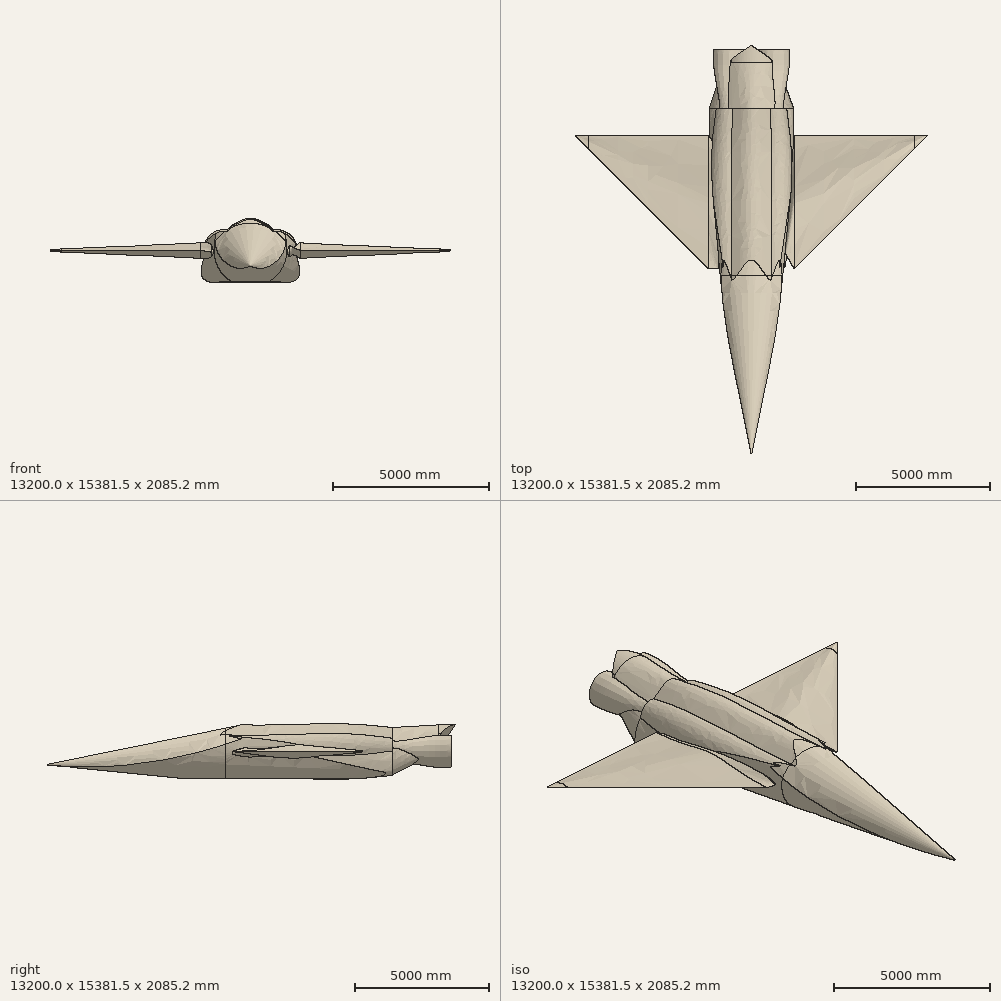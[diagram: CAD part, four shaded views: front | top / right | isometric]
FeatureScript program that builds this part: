
annotation { "Feature Type Name" : "Feature", "Feature Type Description" : "" }
export const myFeature = defineFeature(function(context is Context, id is Id, definition is map)
    precondition{}
    {
        {
            var Q0;
            Q0=qCreatedBy(makeId("Front.planeOp"),FACE);
            cPlane(context, id + "F0", {"entities" : qUnion([Q0]), "cplaneType" : CPlaneType.OFFSET, "offset" : 1750 * mm, "width" : 152.4 * mm, "height" : 152.4 * mm});
        }
        {
            var Q0;
            Q0=qCreatedBy(id+"F0.planeOp",FACE);
            var sketch = newSketch(context, id + "F1", { "sketchPlane" : qUnion([Q0])});
            skLineSegment(sketch, "E0.top", {"start": v(-1394.2, -1000) * mm, "end": v(1394.2, -1000) * mm});
            skPoint(sketch, "E0.middle", {"position": v(0, 0) * mm});
            skFitSpline(sketch, "E1", {"points": [v(-1600, -1000) * mm, v(-848, 530) * mm, v(0, 1000) * mm, v(848, 530) * mm, v(1600, -1000) * mm], "startDerivative": vector(0, 10524.75) * mm, "endDerivative": vector(0, -10524.75) * mm});
            skArc(sketch, "E2", {"start": v(-735.27, 618.52) * mm, "mid": v(-1273.27, 435.52) * mm, "end": v(-1440.68, -107.53) * mm});
            skArc(sketch, "E3.trimOffspring", {"start": v(1440.68, -107.53) * mm, "mid": v(1273.27, 435.52) * mm, "end": v(735.27, 618.52) * mm});
            skFitSpline(sketch, "E4.trimOffspring", {"points": [v(-1600, -1000) * mm, v(-848, 530) * mm, v(0, 1000) * mm, v(848, 530) * mm, v(1600, -1000) * mm], "startDerivative": vector(0, 10524.75) * mm, "endDerivative": vector(0, -10524.75) * mm});
            skFitSpline(sketch, "E5.trimOffspring", {"points": [v(-1600, -1000) * mm, v(-848, 530) * mm, v(0, 1000) * mm, v(848, 530) * mm, v(1600, -1000) * mm], "startDerivative": vector(0, 10524.75) * mm, "endDerivative": vector(0, -10524.75) * mm});
            skArc(sketch, "E6.filletArc", {"start": v(-1593.82, -787.83) * mm, "mid": v(-1539.85, -937.05) * mm, "end": v(-1394.2, -1000) * mm});
            skArc(sketch, "E7.filletArc", {"start": v(1394.2, -1000) * mm, "mid": v(1539.85, -937.05) * mm, "end": v(1593.82, -787.83) * mm});
            skSolve(sketch);
        }
        {
            var Q0;
            Q0=qCreatedBy(makeId("Front.planeOp"),FACE);
            var sketch = newSketch(context, id + "F2", { "sketchPlane" : qUnion([Q0])});
            skLineSegment(sketch, "E8.top", {"start": v(-1394.2, -1000) * mm, "end": v(1394.2, -1000) * mm});
            skPoint(sketch, "E8.middle", {"position": v(0, 0) * mm});
            skFitSpline(sketch, "E9", {"points": [v(-1600, -1000) * mm, v(-848, 530) * mm, v(0, 1000) * mm, v(848, 530) * mm, v(1600, -1000) * mm], "startDerivative": vector(0, 10524.75) * mm, "endDerivative": vector(0, -10524.75) * mm});
            skArc(sketch, "E10", {"start": v(-735.27, 618.52) * mm, "mid": v(-1273.27, 435.52) * mm, "end": v(-1440.68, -107.53) * mm});
            skArc(sketch, "E11.trimOffspring", {"start": v(1440.68, -107.53) * mm, "mid": v(1273.27, 435.52) * mm, "end": v(735.27, 618.52) * mm});
            skFitSpline(sketch, "E12.trimOffspring", {"points": [v(-1600, -1000) * mm, v(-848, 530) * mm, v(0, 1000) * mm, v(848, 530) * mm, v(1600, -1000) * mm], "startDerivative": vector(0, 10524.75) * mm, "endDerivative": vector(0, -10524.75) * mm});
            skFitSpline(sketch, "E13.trimOffspring", {"points": [v(-1600, -1000) * mm, v(-848, 530) * mm, v(0, 1000) * mm, v(848, 530) * mm, v(1600, -1000) * mm], "startDerivative": vector(0, 10524.75) * mm, "endDerivative": vector(0, -10524.75) * mm});
            skArc(sketch, "E14.filletArc", {"start": v(-1593.82, -787.83) * mm, "mid": v(-1539.85, -937.05) * mm, "end": v(-1394.2, -1000) * mm});
            skArc(sketch, "E15.filletArc", {"start": v(1394.2, -1000) * mm, "mid": v(1539.85, -937.05) * mm, "end": v(1593.82, -787.83) * mm});
            skSolve(sketch);
        }
        {
            var Q0;
            Q0=qCreatedBy(makeId("Front.planeOp"),FACE);
            cPlane(context, id + "F3", {"entities" : qUnion([Q0]), "cplaneType" : CPlaneType.OFFSET, "offset" : 3500 * mm, "oppositeDirection" : true, "width" : 150 * mm, "height" : 150 * mm});
        }
        {
            var Q0;
            Q0=qCreatedBy(id+"F3.planeOp",FACE);
            var sketch = newSketch(context, id + "F4", { "sketchPlane" : qUnion([Q0])});
            skLineSegment(sketch, "E16.top", {"start": v(-1394.2, -1000) * mm, "end": v(1394.2, -1000) * mm});
            skPoint(sketch, "E16.middle", {"position": v(0, 0) * mm});
            skFitSpline(sketch, "E17", {"points": [v(-1600, -1000) * mm, v(-848, 530) * mm, v(0, 1000) * mm, v(848, 530) * mm, v(1600, -1000) * mm], "startDerivative": vector(0, 10524.75) * mm, "endDerivative": vector(0, -10524.75) * mm});
            skArc(sketch, "E18", {"start": v(-735.27, 618.52) * mm, "mid": v(-1273.27, 435.52) * mm, "end": v(-1440.68, -107.53) * mm});
            skArc(sketch, "E19.trimOffspring", {"start": v(1440.68, -107.53) * mm, "mid": v(1273.27, 435.52) * mm, "end": v(735.27, 618.52) * mm});
            skFitSpline(sketch, "E20.trimOffspring", {"points": [v(-1600, -1000) * mm, v(-848, 530) * mm, v(0, 1000) * mm, v(848, 530) * mm, v(1600, -1000) * mm], "startDerivative": vector(0, 10524.75) * mm, "endDerivative": vector(0, -10524.75) * mm});
            skFitSpline(sketch, "E21.trimOffspring", {"points": [v(-1600, -1000) * mm, v(-848, 530) * mm, v(0, 1000) * mm, v(848, 530) * mm, v(1600, -1000) * mm], "startDerivative": vector(0, 10524.75) * mm, "endDerivative": vector(0, -10524.75) * mm});
            skArc(sketch, "E22.filletArc", {"start": v(-1593.82, -787.83) * mm, "mid": v(-1539.85, -937.05) * mm, "end": v(-1394.2, -1000) * mm});
            skArc(sketch, "E23.filletArc", {"start": v(1394.2, -1000) * mm, "mid": v(1539.85, -937.05) * mm, "end": v(1593.82, -787.83) * mm});
            skSolve(sketch);
        }
        {
            var Q0;
            Q0=qCreatedBy(makeId("Front.planeOp"),FACE);
            cPlane(context, id + "F5", {"entities" : qUnion([Q0]), "cplaneType" : CPlaneType.OFFSET, "offset" : 4500 * mm, "oppositeDirection" : true, "width" : 150 * mm, "height" : 150 * mm});
        }
        {
            var Q0;
            Q0=qCreatedBy(id+"F5.planeOp",FACE);
            var sketch = newSketch(context, id + "F6", { "sketchPlane" : qUnion([Q0])});
            skLineSegment(sketch, "E24.top", {"start": v(-1413.07, -900) * mm, "end": v(1413.07, -900) * mm});
            skPoint(sketch, "E24.middle", {"position": v(0, 0) * mm});
            skFitSpline(sketch, "E25", {"points": [v(-1600, -900) * mm, v(-784.42, 441.24) * mm, v(0, 900) * mm, v(784.42, 441.24) * mm, v(1600, -900) * mm], "startDerivative": vector(0, 9508.62) * mm, "endDerivative": vector(0, -9508.62) * mm});
            skArc(sketch, "E26", {"start": v(-719.25, 488.69) * mm, "mid": v(-1131.76, 394.84) * mm, "end": v(-1324.66, 18.33) * mm});
            skArc(sketch, "E27.trimOffspring", {"start": v(1324.66, 18.33) * mm, "mid": v(1131.76, 394.84) * mm, "end": v(719.25, 488.69) * mm});
            skFitSpline(sketch, "E28.trimOffspring", {"points": [v(-1600, -900) * mm, v(-784.42, 441.24) * mm, v(0, 900) * mm, v(784.42, 441.24) * mm, v(1600, -900) * mm], "startDerivative": vector(0, 9508.62) * mm, "endDerivative": vector(0, -9508.62) * mm});
            skFitSpline(sketch, "E29.trimOffspring", {"points": [v(-1600, -900) * mm, v(-784.42, 441.24) * mm, v(0, 900) * mm, v(784.42, 441.24) * mm, v(1600, -900) * mm], "startDerivative": vector(0, 9508.62) * mm, "endDerivative": vector(0, -9508.62) * mm});
            skArc(sketch, "E30.filletArc", {"start": v(-1592.48, -705.43) * mm, "mid": v(-1545.4, -842.02) * mm, "end": v(-1413.07, -900) * mm});
            skArc(sketch, "E31.filletArc", {"start": v(1413.07, -900) * mm, "mid": v(1545.4, -842.02) * mm, "end": v(1592.48, -705.43) * mm});
            skLineSegment(sketch, "E32", {"start": v(-719.25, 488.69) * mm, "end": v(-1324.66, 18.33) * mm, "construction": true});
            skLineSegment(sketch, "E33", {"start": v(719.25, 488.69) * mm, "end": v(1324.66, 18.33) * mm, "construction": true});
            skSolve(sketch);
        }
        {
            var Q0;
            Q0=qCreatedBy(makeId("Front.planeOp"),FACE);
            cPlane(context, id + "F7", {"entities" : qUnion([Q0]), "cplaneType" : CPlaneType.OFFSET, "offset" : 6232.05 * mm, "oppositeDirection" : true, "width" : 150 * mm, "height" : 150 * mm});
        }
        {
            var Q0;
            Q0=qCreatedBy(id+"F7.planeOp",FACE);
            var sketch = newSketch(context, id + "F8", { "sketchPlane" : qUnion([Q0])});
            skArc(sketch, "E34", {"start": v(998.61, 52.63) * mm, "mid": v(0, 1000) * mm, "end": v(-998.61, 52.63) * mm});
            skLineSegment(sketch, "E35", {"start": v(0, 0) * mm, "end": v(-948.68, 0) * mm});
            skLineSegment(sketch, "E36", {"start": v(0, 0) * mm, "end": v(948.68, 0) * mm});
            skPoint(sketch, "E37.visualSharp", {"position": v(-1000, 0) * mm});
            skArc(sketch, "E37.filletArc", {"start": v(-998.61, 52.63) * mm, "mid": v(-984.96, 15.59) * mm, "end": v(-948.68, 0) * mm});
            skPoint(sketch, "E38.visualSharp", {"position": v(1000, 0) * mm});
            skArc(sketch, "E38.filletArc", {"start": v(948.68, 0) * mm, "mid": v(984.96, 15.59) * mm, "end": v(998.61, 52.63) * mm});
            skLineSegment(sketch, "E39", {"start": v(0, 1000) * mm, "end": v(0, 675) * mm, "construction": true});
            skPoint(sketch, "E39.endSnap0", {"position": v(0, 1000) * mm});
            skLineSegment(sketch, "E40", {"start": v(0, 675) * mm, "end": v(737.82, 675) * mm, "construction": true});
            skLineSegment(sketch, "E41", {"start": v(0, 675) * mm, "end": v(-737.82, 675) * mm, "construction": true});
            skSolve(sketch);
        }
        {
            var Q0;
            Q0=qSketchRegion(id+"F1",true);
            var Q1;
            Q1=qSketchRegion(id+"F2",true);
            var Q2;
            Q2=qSketchRegion(id+"F4",true);
            var Q3;
            Q3=qSketchRegion(id+"F6",true);
            loft(context, id + "F9", {"sheetProfilesArray" : [{ "sheetProfileEntities" : qUnion([Q0]) }, { "sheetProfileEntities" : qUnion([Q1]) }, { "sheetProfileEntities" : qUnion([Q2]) }, { "sheetProfileEntities" : qUnion([Q3]) }]});
        }
        {
            var Q0;
            Q0=sQuery(id+"F6.wireOp",EDGE,"E32");
            var Q1;
            Q1=sQuery(id+"F8.wireOp",VERTEX,"E41.end");
            cPlane(context, id + "F10", {"entities" : qUnion([Q0, Q1]), "cplaneType" : CPlaneType.LINE_ANGLE, "offset" : 25 * mm, "angle" : 0 * degree, "width" : 150 * mm, "height" : 150 * mm});
        }
        {
            var Q0;
            Q0=qCreatedBy(id+"F10.planeOp",FACE);
            var sketch = newSketch(context, id + "F11", { "sketchPlane" : qUnion([Q0])});
            skLineSegment(sketch, "E42", {"start": v(-589.34, -4526.34) * mm, "end": v(-612.8, -6268.32) * mm});
            skLineSegment(sketch, "E43", {"start": v(-1354.08, -4472.19) * mm, "end": v(-612.8, -6268.32) * mm});
            skSolve(sketch);
        }
        {
            var Q0;
            Q0=sQuery(id+"F6.wireOp",EDGE,"E33");
            var Q1;
            Q1=sQuery(id+"F8.wireOp",VERTEX,"E40.end");
            cPlane(context, id + "F12", {"entities" : qUnion([Q0, Q1]), "cplaneType" : CPlaneType.LINE_ANGLE, "offset" : 25 * mm, "angle" : 0 * degree, "width" : 150 * mm, "height" : 150 * mm});
        }
        {
            var Q0;
            Q0=qCreatedBy(id+"F12.planeOp",FACE);
            var sketch = newSketch(context, id + "F13", { "sketchPlane" : qUnion([Q0])});
            skLineSegment(sketch, "E44", {"start": v(589.34, 4526.34) * mm, "end": v(612.8, 6268.32) * mm});
            skLineSegment(sketch, "E45", {"start": v(1354.08, 4472.19) * mm, "end": v(612.8, 6268.32) * mm});
            skSolve(sketch);
        }
        {
            var Q1;
            Q1=makeQuery(id+"F6.imprint","IMPRINT",FACE,{"disambiguationData":[TD([[makeQuery(id+"F6.imprint","IMPRINT",EDGE,{"derivedFrom":sQuery(id+"F6.wireOp",EDGE,"E24.top")}),1.0]])]});
            var Q2;
            Q2=makeQuery(id+"F8.imprint","IMPRINT",FACE,{"disambiguationData":[TD([[makeQuery(id+"F8.imprint","IMPRINT",EDGE,{"derivedFrom":sQuery(id+"F8.wireOp",EDGE,"E34")}),1.0]])]});
            var Q3;
            Q3=sQuery(id+"F11.wireOp",EDGE,"E42");
            var Q4;
            Q4=sQuery(id+"F13.wireOp",EDGE,"E44");
            loft(context, id + "F14", {"operationType" : NewBodyOperationType.ADD, "addGuides" : true, "sheetProfilesArray" : [{ "sheetProfileEntities" : qUnion([Q1]) }, { "sheetProfileEntities" : qUnion([Q2]) }], "guidesArray" : [{ "guideEntities" : qUnion([Q3]), "guideDerivativeType" : LoftGuideDerivativeType.DEFAULT, "guideDerivativeMagnitude" : 1 }, { "guideEntities" : qUnion([Q4]), "guideDerivativeType" : LoftGuideDerivativeType.DEFAULT, "guideDerivativeMagnitude" : 1 }]});
        }
        {
            var Q0;
            Q0=makeQuery(id+"F14.opLoft","CAP_FACE",FACE,{"disambiguationData":[OSD([makeQuery(id+"F8.imprint","IMPRINT",FACE,{"disambiguationData":[TD([[makeQuery(id+"F8.imprint","IMPRINT",EDGE,{"derivedFrom":sQuery(id+"F8.wireOp",EDGE,"E34")}),1.0]])]})])],"isStart":true});
            extrude(context, id + "F15", {"entities" : qUnion([Q0]), "operationType" : NewBodyOperationType.ADD, "depth" : 649.4 * mm});
        }
        {
            var Q0;
            Q0=qCreatedBy(makeId("Right.planeOp"),FACE);
            var sketch = newSketch(context, id + "F16", { "sketchPlane" : qUnion([Q0])});
            skLineSegment(sketch, "E46", {"start": v(0, 0) * mm, "end": v(4500, 0) * mm});
            skLineSegment(sketch, "E47", {"start": v(4500, 0) * mm, "end": v(6232.05, 0) * mm});
            skLineSegment(sketch, "E48", {"start": v(4500, 0) * mm, "end": v(4500, 1000) * mm});
            skLineSegment(sketch, "E49", {"start": v(4500, 1000) * mm, "end": v(6881.46, 1000) * mm});
            skLineSegment(sketch, "E50", {"start": v(6881.46, 1000) * mm, "end": v(6881.46, -1000) * mm});
            skLineSegment(sketch, "E51", {"start": v(6881.46, 1000) * mm, "end": v(6232.05, 0) * mm});
            skLineSegment(sketch, "E52", {"start": v(6232.05, 0) * mm, "end": v(5582.64, -1000) * mm});
            skLineSegment(sketch, "E53", {"start": v(5582.64, -1000) * mm, "end": v(6881.46, -1000) * mm});
            skSolve(sketch);
        }
        {
            var Q0;
            Q0=makeQuery(id+"F16.imprint","IMPRINT",FACE,{"disambiguationData":[TD([[makeQuery(id+"F16.imprint","IMPRINT",EDGE,{"derivedFrom":sQuery(id+"F16.wireOp",EDGE,"E50")}),-1.0]])]});
            var Q1;
            Q1=sQuery(id+"F16.wireOp",EDGE,"E49");
            revolve(context, id + "F17", {"operationType" : NewBodyOperationType.REMOVE, "entities" : qUnion([Q0]), "axis" : qUnion([Q1]), "revolveType" : RevolveType.SYMMETRIC, "oppositeDirection" : true, "angle" : 182 * degree});
        }
        {
            var Q0;
            Q0=makeQuery(id+"F9.opLoft","CAP_FACE",FACE,{"disambiguationData":[OSD([makeQuery(id+"F1.imprint","IMPRINT",FACE,{"disambiguationData":[TD([[makeQuery(id+"F1.imprint","IMPRINT",EDGE,{"derivedFrom":sQuery(id+"F1.wireOp",EDGE,"E0.top")}),1.0]])]})])],"isStart":true});
            extrude(context, id + "F18", {"entities" : qUnion([Q0]), "depth" : 6750 * mm});
        }
        {
            var Q0;
            Q0=qCreatedBy(makeId("Right.planeOp"),FACE);
            var sketch = newSketch(context, id + "F19", { "sketchPlane" : qUnion([Q0])});
            skLineSegment(sketch, "E54", {"start": v(0, 0) * mm, "end": v(-3500, 0) * mm});
            skLineSegment(sketch, "E55", {"start": v(-3500, 0) * mm, "end": v(-3500, -1000) * mm});
            skLineSegment(sketch, "E56", {"start": v(-3500, -1000) * mm, "end": v(-8500, -1000) * mm});
            skLineSegment(sketch, "E57", {"start": v(-8500, -1000) * mm, "end": v(-8500, -499.31) * mm});
            skLineSegment(sketch, "E58", {"start": v(-1151.4, 0) * mm, "end": v(-1151.4, 1000) * mm});
            skLineSegment(sketch, "E59", {"start": v(-1151.4, 1000) * mm, "end": v(-8500, -499.31) * mm});
            skLineSegment(sketch, "E60", {"start": v(-8500, -499.31) * mm, "end": v(-3500, -1000) * mm});
            skLineSegment(sketch, "E61", {"start": v(-1151.4, 1000) * mm, "end": v(-8500, 1000) * mm});
            skLineSegment(sketch, "E62", {"start": v(-8500, 1000) * mm, "end": v(-8500, -499.31) * mm});
            skLineSegment(sketch, "E63", {"start": v(-8500, -1000) * mm, "end": v(-8500, -1980) * mm});
            skLineSegment(sketch, "E64", {"start": v(-3500, -1000) * mm, "end": v(6286.5, -1980) * mm});
            skLineSegment(sketch, "E65", {"start": v(6286.5, -1980) * mm, "end": v(-8500, -1980) * mm});
            skLineSegment(sketch, "E66", {"start": v(-8500, -499.31) * mm, "end": v(-3500, -499.31) * mm});
            skSolve(sketch);
        }
        {
            var Q0;
            Q0=makeQuery(id+"F19.imprint","IMPRINT",FACE,{"disambiguationData":[TD([[makeQuery(id+"F19.imprint","IMPRINT",EDGE,{"derivedFrom":sQuery(id+"F19.wireOp",EDGE,"E59")}),-1.0]])]});
            var Q1;
            Q1=sQuery(id+"F19.wireOp",EDGE,"E66");
            revolve(context, id + "F20", {"operationType" : NewBodyOperationType.REMOVE, "entities" : qUnion([Q0]), "axis" : qUnion([Q1]), "revolveType" : RevolveType.SYMMETRIC, "oppositeDirection" : true, "angle" : 250 * degree});
        }
        {
            var Q0;
            Q0=makeQuery(id+"F19.imprint","IMPRINT",FACE,{"disambiguationData":[TD([[makeQuery(id+"F19.imprint","IMPRINT",EDGE,{"derivedFrom":sQuery(id+"F19.wireOp",EDGE,"E56")}),-1.0]])]});
            var Q1;
            Q1=makeQuery(id+"F19.imprint","IMPRINT",FACE,{"disambiguationData":[TD([[makeQuery(id+"F19.imprint","IMPRINT",EDGE,{"derivedFrom":sQuery(id+"F19.wireOp",EDGE,"E56")}),1.0]])]});
            var Q2;
            Q2=sQuery(id+"F19.wireOp",EDGE,"E54");
            revolve(context, id + "F21", {"operationType" : NewBodyOperationType.REMOVE, "entities" : qUnion([Q0, Q1]), "axis" : qUnion([Q2]), "revolveType" : RevolveType.SYMMETRIC, "oppositeDirection" : true, "angle" : 240 * degree});
        }
        {
            var Q0;
            Q0=qCreatedBy(makeId("Front.planeOp"),FACE);
            cPlane(context, id + "F22", {"entities" : qUnion([Q0]), "cplaneType" : CPlaneType.OFFSET, "offset" : 3500 * mm, "oppositeDirection" : true, "width" : 150 * mm, "height" : 150 * mm});
        }
        {
            var Q0;
            Q0=qCreatedBy(id+"F22.planeOp",FACE);
            var sketch = newSketch(context, id + "F23", { "sketchPlane" : qUnion([Q0])});
            skCircle(sketch, "E67", {"center": v(-825, 0) * mm, "radius": 600 * mm});
            skCircle(sketch, "E68", {"center": v(825, 0) * mm, "radius": 600 * mm});
            skSolve(sketch);
        }
        {
            var Q0;
            Q0=qCreatedBy(makeId("Front.planeOp"),FACE);
            cPlane(context, id + "F24", {"entities" : qUnion([Q0]), "cplaneType" : CPlaneType.OFFSET, "offset" : 4500 * mm, "oppositeDirection" : true, "width" : 150 * mm, "height" : 150 * mm});
        }
        {
            var Q0;
            Q0=qCreatedBy(id+"F24.planeOp",FACE);
            var sketch = newSketch(context, id + "F25", { "sketchPlane" : qUnion([Q0])});
            skCircle(sketch, "E69", {"center": v(-825, 0) * mm, "radius": 400 * mm});
            skCircle(sketch, "E70", {"center": v(825, 0) * mm, "radius": 400 * mm});
            skSolve(sketch);
        }
        {
            var Q0;
            Q0=qCreatedBy(makeId("Front.planeOp"),FACE);
            cPlane(context, id + "F26", {"entities" : qUnion([Q0]), "cplaneType" : CPlaneType.OFFSET, "offset" : 6232.05 * mm, "oppositeDirection" : true, "width" : 150 * mm, "height" : 150 * mm});
        }
        {
            var Q0;
            Q0=qCreatedBy(id+"F26.planeOp",FACE);
            var sketch = newSketch(context, id + "F27", { "sketchPlane" : qUnion([Q0])});
            skCircle(sketch, "E71", {"center": v(-825, 0) * mm, "radius": 600 * mm});
            skCircle(sketch, "E72", {"center": v(825, 0) * mm, "radius": 600 * mm});
            skSolve(sketch);
        }
        {
            var Q0;
            Q0=qCreatedBy(makeId("Front.planeOp"),FACE);
            cPlane(context, id + "F28", {"entities" : qUnion([Q0]), "cplaneType" : CPlaneType.OFFSET, "offset" : 6732.05 * mm, "oppositeDirection" : true, "width" : 150 * mm, "height" : 150 * mm});
        }
        {
            var Q0;
            Q0=qCreatedBy(id+"F28.planeOp",FACE);
            var sketch = newSketch(context, id + "F29", { "sketchPlane" : qUnion([Q0])});
            skCircle(sketch, "E73", {"center": v(-825, 0) * mm, "radius": 600 * mm});
            skCircle(sketch, "E74", {"center": v(825, 0) * mm, "radius": 600 * mm});
            skSolve(sketch);
        }
        {
            var Q0;
            Q0=makeQuery(id+"F23.imprint","IMPRINT",FACE,{"disambiguationData":[TD([[makeQuery(id+"F23.imprint","IMPRINT",EDGE,{"derivedFrom":sQuery(id+"F23.wireOp",EDGE,"E67")}),1.0]])]});
            var Q1;
            Q1=makeQuery(id+"F25.imprint","IMPRINT",FACE,{"disambiguationData":[TD([[makeQuery(id+"F25.imprint","IMPRINT",EDGE,{"derivedFrom":sQuery(id+"F25.wireOp",EDGE,"E69")}),1.0]])]});
            var Q2;
            Q2=makeQuery(id+"F27.imprint","IMPRINT",FACE,{"disambiguationData":[TD([[makeQuery(id+"F27.imprint","IMPRINT",EDGE,{"derivedFrom":sQuery(id+"F27.wireOp",EDGE,"E71")}),1.0]])]});
            var Q3;
            Q3=makeQuery(id+"F29.imprint","IMPRINT",FACE,{"disambiguationData":[TD([[makeQuery(id+"F29.imprint","IMPRINT",EDGE,{"derivedFrom":sQuery(id+"F29.wireOp",EDGE,"E73")}),1.0]])]});
            loft(context, id + "F30", {"sheetProfilesArray" : [{ "sheetProfileEntities" : qUnion([Q0]) }, { "sheetProfileEntities" : qUnion([Q1]) }, { "sheetProfileEntities" : qUnion([Q2]) }, { "sheetProfileEntities" : qUnion([Q3]) }]});
        }
        {
            var Q0;
            Q0=makeQuery(id+"F23.imprint","IMPRINT",FACE,{"disambiguationData":[TD([[makeQuery(id+"F23.imprint","IMPRINT",EDGE,{"derivedFrom":sQuery(id+"F23.wireOp",EDGE,"E68")}),1.0]])]});
            var Q1;
            Q1=makeQuery(id+"F25.imprint","IMPRINT",FACE,{"disambiguationData":[TD([[makeQuery(id+"F25.imprint","IMPRINT",EDGE,{"derivedFrom":sQuery(id+"F25.wireOp",EDGE,"E70")}),1.0]])]});
            var Q2;
            Q2=makeQuery(id+"F27.imprint","IMPRINT",FACE,{"disambiguationData":[TD([[makeQuery(id+"F27.imprint","IMPRINT",EDGE,{"derivedFrom":sQuery(id+"F27.wireOp",EDGE,"E72")}),1.0]])]});
            var Q3;
            Q3=makeQuery(id+"F29.imprint","IMPRINT",FACE,{"disambiguationData":[TD([[makeQuery(id+"F29.imprint","IMPRINT",EDGE,{"derivedFrom":sQuery(id+"F29.wireOp",EDGE,"E74")}),1.0]])]});
            loft(context, id + "F31", {"sheetProfilesArray" : [{ "sheetProfileEntities" : qUnion([Q0]) }, { "sheetProfileEntities" : qUnion([Q1]) }, { "sheetProfileEntities" : qUnion([Q2]) }, { "sheetProfileEntities" : qUnion([Q3]) }]});
        }
        {
            var Q0;
            Q0=qCreatedBy(makeId("Top.planeOp"),FACE);
            var sketch = newSketch(context, id + "F32", { "sketchPlane" : qUnion([Q0])});
            skLineSegment(sketch, "E75", {"start": v(0, 0) * mm, "end": v(0, 1000) * mm});
            skLineSegment(sketch, "E76", {"start": v(0, 1000) * mm, "end": v(-1600, 1000) * mm});
            skLineSegment(sketch, "E77", {"start": v(-1600, 1000) * mm, "end": v(-1600, -1500) * mm});
            skLineSegment(sketch, "E78", {"start": v(-1600, 1000) * mm, "end": v(-1600, 3500) * mm});
            skLineSegment(sketch, "E79", {"start": v(-1600, 3500) * mm, "end": v(-6100, 3500) * mm});
            skLineSegment(sketch, "E80", {"start": v(-6100, 3500) * mm, "end": v(-6600, 3500) * mm});
            skLineSegment(sketch, "E81", {"start": v(-6100, 3500) * mm, "end": v(-6100, 3000) * mm});
            skLineSegment(sketch, "E82", {"start": v(-1600, -1500) * mm, "end": v(-6100, 3000) * mm});
            skLineSegment(sketch, "E83", {"start": v(0, 1000) * mm, "end": v(1600, 1000) * mm});
            skLineSegment(sketch, "E84", {"start": v(1600, 1000) * mm, "end": v(1600, -1500) * mm});
            skLineSegment(sketch, "E85", {"start": v(1600, 1000) * mm, "end": v(1600, 3500) * mm});
            skLineSegment(sketch, "E86", {"start": v(1600, 3500) * mm, "end": v(6100, 3500) * mm});
            skLineSegment(sketch, "E87", {"start": v(6100, 3500) * mm, "end": v(6600, 3500) * mm});
            skLineSegment(sketch, "E88", {"start": v(6100, 3500) * mm, "end": v(6100, 3000) * mm});
            skLineSegment(sketch, "E89", {"start": v(1600, -1500) * mm, "end": v(6100, 3000) * mm});
            skSolve(sketch);
        }
        {
            var Q0;
            Q0=qCreatedBy(makeId("Right.planeOp"),FACE);
            var sketch = newSketch(context, id + "F33", { "sketchPlane" : qUnion([Q0])});
            skFitSpline(sketch, "E90", {"points": [v(-1500, -50) * mm, v(0, 250) * mm, v(3000, -50) * mm, v(0, -250) * mm, v(-1500, -50) * mm]});
            skSolve(sketch);
        }
        {
            var Q0;
            Q0=qCreatedBy(makeId("Right.planeOp"),FACE);
            cPlane(context, id + "F34", {"entities" : qUnion([Q0]), "cplaneType" : CPlaneType.OFFSET, "offset" : 1600 * mm, "oppositeDirection" : true, "width" : 150 * mm, "height" : 150 * mm});
        }
        {
            var Q0;
            Q0=qCreatedBy(id+"F34.planeOp",FACE);
            var sketch = newSketch(context, id + "F35", { "sketchPlane" : qUnion([Q0])});
            skFitSpline(sketch, "E91", {"points": [v(-1500, 0) * mm, v(1000, 250) * mm, v(3500, 0) * mm], "startDerivative": vector(7500, 0) * mm, "endDerivative": vector(7500, 0) * mm});
            skFitSpline(sketch, "E92", {"points": [v(-1500, 0) * mm, v(1000, -250) * mm, v(3500, 0) * mm], "startDerivative": vector(5000, -750) * mm, "endDerivative": vector(7500, 0) * mm});
            skSolve(sketch);
        }
        {
            var Q0;
            Q0=qCreatedBy(makeId("Right.planeOp"),FACE);
            cPlane(context, id + "F36", {"entities" : qUnion([Q0]), "cplaneType" : CPlaneType.OFFSET, "offset" : 1600 * mm, "width" : 150 * mm, "height" : 150 * mm});
        }
        {
            var Q0;
            Q0=qCreatedBy(id+"F36.planeOp",FACE);
            var sketch = newSketch(context, id + "F37", { "sketchPlane" : qUnion([Q0])});
            skFitSpline(sketch, "E93", {"points": [v(-1500, 0) * mm, v(1000, 250) * mm, v(3500, 0) * mm], "startDerivative": vector(7500, 0) * mm, "endDerivative": vector(7500, 0) * mm});
            skFitSpline(sketch, "E94", {"points": [v(-1500, 0) * mm, v(1000, -250) * mm, v(3500, 0) * mm], "startDerivative": vector(5000, -750) * mm, "endDerivative": vector(7500, 0) * mm});
            skSolve(sketch);
        }
        {
            var Q0;
            Q0=qCreatedBy(makeId("Right.planeOp"),FACE);
            cPlane(context, id + "F38", {"entities" : qUnion([Q0]), "cplaneType" : CPlaneType.OFFSET, "offset" : 6100 * mm, "oppositeDirection" : true, "width" : 150 * mm, "height" : 150 * mm});
        }
        {
            var Q0;
            Q0=qCreatedBy(id+"F38.planeOp",FACE);
            var sketch = newSketch(context, id + "F39", { "sketchPlane" : qUnion([Q0])});
            skFitSpline(sketch, "E95", {"points": [v(3000, 0) * mm, v(3250, 50) * mm, v(3500, 0) * mm], "startDerivative": vector(750, 0) * mm, "endDerivative": vector(750, 0) * mm});
            skFitSpline(sketch, "E96", {"points": [v(3000, 0) * mm, v(3250, -50) * mm, v(3500, 0) * mm], "startDerivative": vector(500, -150) * mm, "endDerivative": vector(750, 0) * mm});
            skSolve(sketch);
        }
        {
            var Q0;
            Q0=qCreatedBy(makeId("Right.planeOp"),FACE);
            cPlane(context, id + "F40", {"entities" : qUnion([Q0]), "cplaneType" : CPlaneType.OFFSET, "offset" : 6100 * mm, "width" : 150 * mm, "height" : 150 * mm});
        }
        {
            var Q0;
            Q0=qCreatedBy(id+"F40.planeOp",FACE);
            var sketch = newSketch(context, id + "F41", { "sketchPlane" : qUnion([Q0])});
            skFitSpline(sketch, "E97", {"points": [v(3000, 0) * mm, v(3250, 50) * mm, v(3500, 0) * mm], "startDerivative": vector(850.99, 0) * mm, "endDerivative": vector(750, 0) * mm});
            skFitSpline(sketch, "E98", {"points": [v(3000, 0) * mm, v(3250, -50) * mm, v(3500, 0) * mm], "startDerivative": vector(500, -150) * mm, "endDerivative": vector(750, 0) * mm});
            skSolve(sketch);
        }
        {
            var Q0;
            Q0 = qSketchRegion(id + "F33", true);
            extrude(context, id + "F42", {"entities" : qUnion([Q0]), "endBound" : BoundingType.SYMMETRIC, "depth" : 2500 * mm});
        }
        {
            var Q1;
            Q1=makeQuery(id+"F42.opExtrude","CAP_FACE",FACE,{"disambiguationData":[OSD([sQuery(id+"F33.wireOp",EDGE,"E90")])],"isStart":true});
            var Q2;
            {var subQ0=sQuery(id+"F35.wireOp",EDGE,"E91");Q2=makeQuery(id+"F35.imprint","IMPRINT",FACE,{"disambiguationData":[TD([[makeQuery(id+"F35.imprint","IMPRINT",EDGE,{"derivedFrom":subQ0}),-1.0]])]});}
            loft(context, id + "F43", {"operationType" : NewBodyOperationType.ADD, "sheetProfilesArray" : [{ "sheetProfileEntities" : qUnion([Q1]) }, { "sheetProfileEntities" : qUnion([Q2]) }]});
        }
        {
            var Q1;
            Q1=makeQuery(id+"F42.opExtrude","CAP_FACE",FACE,{"disambiguationData":[OSD([sQuery(id+"F33.wireOp",EDGE,"E90")])],"isStart":false});
            var Q2;
            {var subQ0=sQuery(id+"F37.wireOp",EDGE,"E93");Q2=makeQuery(id+"F37.imprint","IMPRINT",FACE,{"disambiguationData":[TD([[makeQuery(id+"F37.imprint","IMPRINT",EDGE,{"derivedFrom":subQ0}),-1.0]])]});}
            loft(context, id + "F44", {"operationType" : NewBodyOperationType.ADD, "sheetProfilesArray" : [{ "sheetProfileEntities" : qUnion([Q1]) }, { "sheetProfileEntities" : qUnion([Q2]) }]});
        }
        {
            var Q1;
            {var subQ0=sQuery(id+"F35.wireOp",EDGE,"E91");Q1=makeQuery(id+"F43.opLoft","CAP_FACE",FACE,{"disambiguationData":[OSD([makeQuery(id+"F35.imprint","IMPRINT",FACE,{"disambiguationData":[TD([[makeQuery(id+"F35.imprint","IMPRINT",EDGE,{"derivedFrom":subQ0}),-1.0]])]})])],"isStart":true});}
            var Q2;
            {var subQ0=sQuery(id+"F39.wireOp",EDGE,"E95");Q2=makeQuery(id+"F39.imprint","IMPRINT",FACE,{"disambiguationData":[TD([[makeQuery(id+"F39.imprint","IMPRINT",EDGE,{"derivedFrom":subQ0}),-1.0]])]});}
            loft(context, id + "F45", {"operationType" : NewBodyOperationType.ADD, "sheetProfilesArray" : [{ "sheetProfileEntities" : qUnion([Q1]) }, { "sheetProfileEntities" : qUnion([Q2]) }]});
        }
        {
            var Q1;
            {var subQ0=sQuery(id+"F37.wireOp",EDGE,"E93");Q1=makeQuery(id+"F44.opLoft","CAP_FACE",FACE,{"disambiguationData":[OSD([makeQuery(id+"F37.imprint","IMPRINT",FACE,{"disambiguationData":[TD([[makeQuery(id+"F37.imprint","IMPRINT",EDGE,{"derivedFrom":subQ0}),-1.0]])]})])],"isStart":true});}
            var Q2;
            {var subQ0=sQuery(id+"F41.wireOp",EDGE,"E97");Q2=makeQuery(id+"F41.imprint","IMPRINT",FACE,{"disambiguationData":[TD([[makeQuery(id+"F41.imprint","IMPRINT",EDGE,{"derivedFrom":subQ0}),-1.0]])]});}
            loft(context, id + "F46", {"operationType" : NewBodyOperationType.ADD, "sheetProfilesArray" : [{ "sheetProfileEntities" : qUnion([Q1]) }, { "sheetProfileEntities" : qUnion([Q2]) }]});
        }
        {
            var Q1;
            {var subQ0=sQuery(id+"F39.wireOp",EDGE,"E95");Q1=makeQuery(id+"F45.opLoft","CAP_FACE",FACE,{"disambiguationData":[OSD([makeQuery(id+"F39.imprint","IMPRINT",FACE,{"disambiguationData":[TD([[makeQuery(id+"F39.imprint","IMPRINT",EDGE,{"derivedFrom":subQ0}),-1.0]])]})])],"isStart":true});}
            var Q2;
            Q2=sQuery(id+"F32.wireOp",VERTEX,"E80.end");
            loft(context, id + "F47", {"operationType" : NewBodyOperationType.ADD, "sheetProfilesArray" : [{ "sheetProfileEntities" : qUnion([Q1]) }, { "sheetProfileEntities" : qUnion([Q2]) }]});
        }
        {
            var Q1;
            {var subQ0=sQuery(id+"F41.wireOp",EDGE,"E97");Q1=makeQuery(id+"F46.opLoft","CAP_FACE",FACE,{"disambiguationData":[OSD([makeQuery(id+"F41.imprint","IMPRINT",FACE,{"disambiguationData":[TD([[makeQuery(id+"F41.imprint","IMPRINT",EDGE,{"derivedFrom":subQ0}),-1.0]])]})])],"isStart":true});}
            var Q2;
            Q2=sQuery(id+"F32.wireOp",VERTEX,"E87.end");
            loft(context, id + "F48", {"operationType" : NewBodyOperationType.ADD, "sheetProfilesArray" : [{ "sheetProfileEntities" : qUnion([Q1]) }, { "sheetProfileEntities" : qUnion([Q2]) }]});
        }
    });
